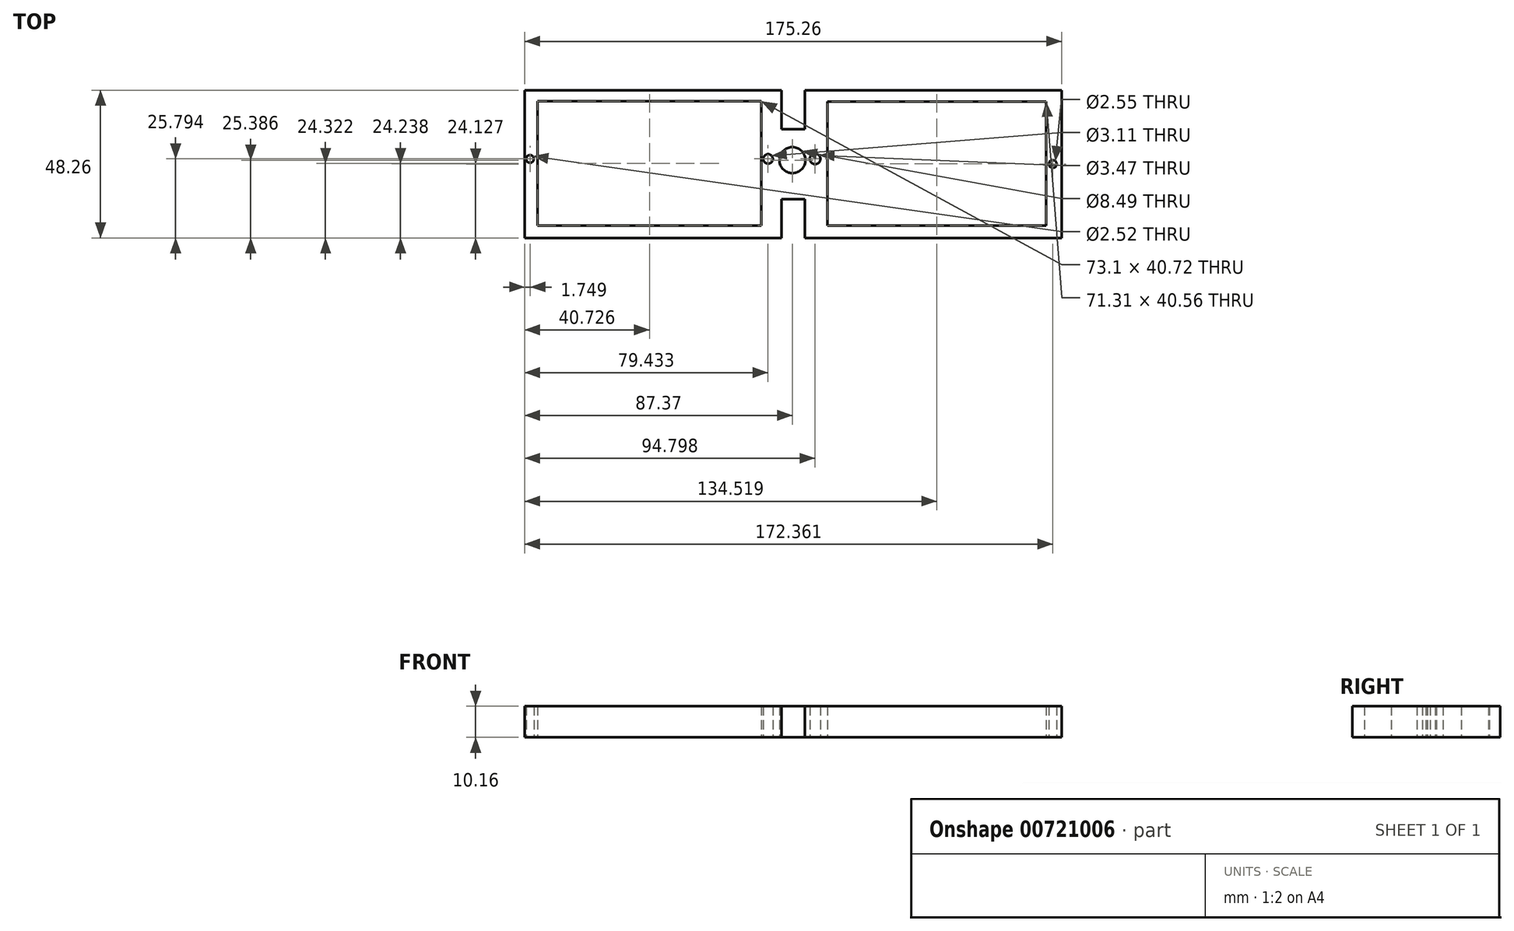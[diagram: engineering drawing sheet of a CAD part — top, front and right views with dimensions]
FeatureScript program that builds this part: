
annotation { "Feature Type Name" : "Feature", "Feature Type Description" : "" }
export const myFeature = defineFeature(function(context is Context, id is Id, definition is map)
    precondition{}
    {
        {
            var Q0;
            Q0=qCreatedBy(makeId("Top.planeOp"),FACE);
            var sketch = newSketch(context, id + "F0", { "sketchPlane" : qUnion([Q0])});
            skLineSegment(sketch, "E0", {"start": v(-69.5, 31.23) * mm, "end": v(14.31, 31.23) * mm});
            skLineSegment(sketch, "E1", {"start": v(14.31, 31.23) * mm, "end": v(14.31, 18.53) * mm});
            skLineSegment(sketch, "E2", {"start": v(14.31, 18.53) * mm, "end": v(21.93, 18.53) * mm});
            skLineSegment(sketch, "E3", {"start": v(21.93, 18.53) * mm, "end": v(21.93, 31.23) * mm});
            skLineSegment(sketch, "E4", {"start": v(21.93, 31.23) * mm, "end": v(105.75, 31.23) * mm});
            skLineSegment(sketch, "E5", {"start": v(105.75, 31.23) * mm, "end": v(105.75, -17.03) * mm});
            skLineSegment(sketch, "E6", {"start": v(105.75, -17.03) * mm, "end": v(21.93, -17.03) * mm});
            skLineSegment(sketch, "E7", {"start": v(21.93, -17.03) * mm, "end": v(21.93, -4.33) * mm});
            skLineSegment(sketch, "E8", {"start": v(21.93, -4.33) * mm, "end": v(14.31, -4.33) * mm});
            skLineSegment(sketch, "E9", {"start": v(14.31, -4.33) * mm, "end": v(14.31, -17.03) * mm});
            skLineSegment(sketch, "E10", {"start": v(14.31, -17.03) * mm, "end": v(-69.5, -17.03) * mm});
            skLineSegment(sketch, "E11", {"start": v(-69.5, -17.03) * mm, "end": v(-69.5, 31.23) * mm});
            skLineSegment(sketch, "E12", {"start": v(-65.34, 27.65) * mm, "end": v(-65.34, -13.07) * mm});
            skLineSegment(sketch, "E13", {"start": v(-65.34, -13.07) * mm, "end": v(7.77, -13.07) * mm});
            skLineSegment(sketch, "E14", {"start": v(7.77, -13.07) * mm, "end": v(7.77, 0) * mm});
            skLineSegment(sketch, "E15", {"start": v(29.35, 0) * mm, "end": v(29.35, -13.07) * mm});
            skLineSegment(sketch, "E16", {"start": v(29.35, -13.07) * mm, "end": v(100.66, -13.07) * mm});
            skLineSegment(sketch, "E17", {"start": v(100.66, -13.07) * mm, "end": v(100.66, 27.49) * mm});
            skLineSegment(sketch, "E18", {"start": v(100.66, 27.49) * mm, "end": v(29.35, 27.49) * mm});
            skLineSegment(sketch, "E19", {"start": v(29.35, 27.49) * mm, "end": v(29.35, 14.53) * mm});
            skLineSegment(sketch, "E20", {"start": v(7.77, 14.53) * mm, "end": v(7.77, 27.65) * mm});
            skLineSegment(sketch, "E21", {"start": v(7.77, 27.65) * mm, "end": v(-65.34, 27.65) * mm});
            skLineSegment(sketch, "E22", {"start": v(7.77, 14.53) * mm, "end": v(7.77, 0) * mm});
            skLineSegment(sketch, "E23", {"start": v(29.35, 14.53) * mm, "end": v(29.35, 0) * mm});
            skCircle(sketch, "E24", {"center": v(17.86, 8.36) * mm, "radius": 4.25 * mm});
            skCircle(sketch, "E25", {"center": v(25.29, 8.76) * mm, "radius": 1.73 * mm});
            skCircle(sketch, "E26", {"center": v(9.92, 8.76) * mm, "radius": 1.55 * mm});
            skCircle(sketch, "E27", {"center": v(102.85, 7.1) * mm, "radius": 1.27 * mm});
            skPoint(sketch, "E27.centerSnap0", {"position": v(105.75, 7.1) * mm});
            skCircle(sketch, "E28", {"center": v(-67.76, 8.76) * mm, "radius": 1.26 * mm});
            skSolve(sketch);
        }
        {
            var Q0;
            Q0 = qSketchRegion(id + "F0", true);
            extrude(context, id + "F1", {"entities" : qUnion([Q0]), "depth" : 10.16 * mm, "offsetDistance" : 25.4 * mm});
        }
    });
